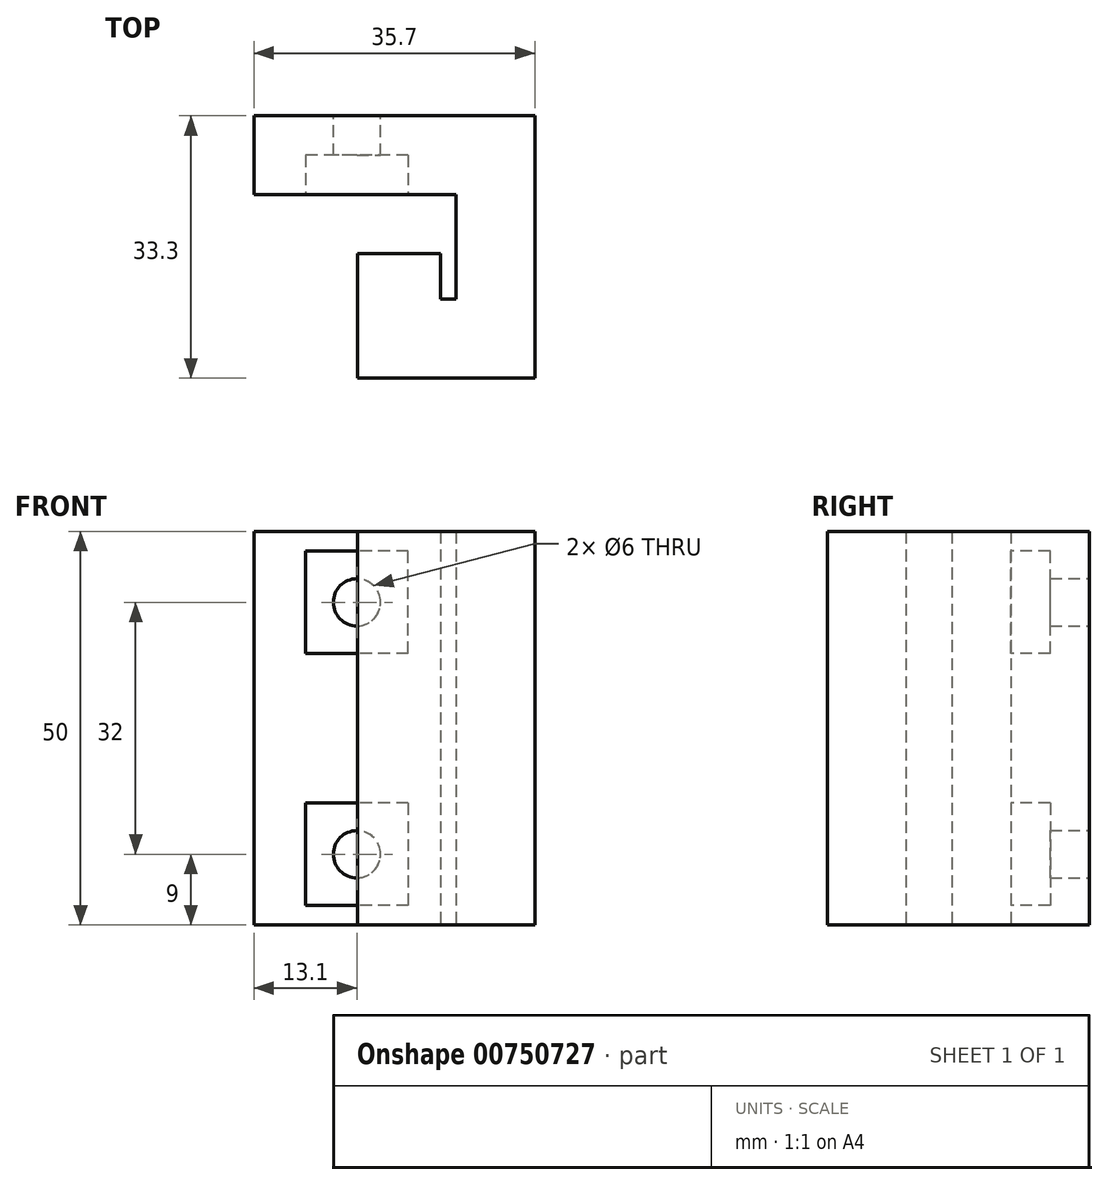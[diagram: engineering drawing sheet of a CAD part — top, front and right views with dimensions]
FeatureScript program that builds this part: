
annotation { "Feature Type Name" : "Feature", "Feature Type Description" : "" }
export const myFeature = defineFeature(function(context is Context, id is Id, definition is map)
    precondition{}
    {
        {
            var Q0;
            Q0=qCreatedBy(makeId("Top.planeOp"),FACE);
            var sketch = newSketch(context, id + "F0", { "sketchPlane" : qUnion([Q0])});
            skPoint(sketch, "E0.middle", {"position": v(0, 0) * mm});
            skLineSegment(sketch, "E1", {"start": v(22.5, 33.3) * mm, "end": v(22.5, 0) * mm});
            skLineSegment(sketch, "E2", {"start": v(22.5, 0) * mm, "end": v(0, 0) * mm});
            skLineSegment(sketch, "E3", {"start": v(12.5, 10) * mm, "end": v(12.5, 23.3) * mm});
            skLineSegment(sketch, "E4", {"start": v(12.5, 23.3) * mm, "end": v(-13.2, 23.3) * mm});
            skLineSegment(sketch, "E5", {"start": v(12.5, 10) * mm, "end": v(10.5, 10) * mm});
            skLineSegment(sketch, "E6", {"start": v(10.5, 10) * mm, "end": v(10.5, 15.8) * mm});
            skLineSegment(sketch, "E7", {"start": v(10.5, 15.8) * mm, "end": v(0, 15.8) * mm});
            skLineSegment(sketch, "E8", {"start": v(0, 15.8) * mm, "end": v(0, 0) * mm});
            skLineSegment(sketch, "E9", {"start": v(22.5, 33.3) * mm, "end": v(-13.2, 33.3) * mm});
            skLineSegment(sketch, "E10", {"start": v(22.5, 16.65) * mm, "end": v(12.5, 16.65) * mm, "construction": true});
            skLineSegment(sketch, "E11", {"start": v(11.5, 10) * mm, "end": v(11.5, 0) * mm, "construction": true});
            skLineSegment(sketch, "E12", {"start": v(-13.2, 33.3) * mm, "end": v(-13.2, 23.3) * mm});
            skSolve(sketch);
        }
        {
            var Q0;
            Q0 = qSketchRegion(id + "F0", true);
            extrude(context, id + "F1", {"entities" : qUnion([Q0]), "endBound" : BoundingType.SYMMETRIC, "depth" : 50 * mm, "offsetDistance" : 25 * mm});
        }
        {
            var Q0;
            Q0=makeQuery(id+"F1.opExtrude","SWEPT_FACE",FACE,{"disambiguationData":[OSD([sQuery(id+"F0.wireOp",EDGE,"E9")])]});
            var sketch = newSketch(context, id + "F2", { "sketchPlane" : qUnion([Q0])});
            skCircle(sketch, "E13", {"center": v(0.1, -16) * mm, "radius": 3 * mm});
            skCircle(sketch, "E14.MirrorC", {"center": v(0.1, 16) * mm, "radius": 3 * mm});
            skSolve(sketch);
        }
        {
            var Q0;
            Q0 = qSketchRegion(id + "F2", true);
            var Q1;
            Q1=makeQuery(id+"F1.opExtrude","SWEPT_FACE",FACE,{"disambiguationData":[OSD([sQuery(id+"F0.wireOp",EDGE,"E4")])]});
            extrude(context, id + "F3", {"entities" : qUnion([Q0]), "operationType" : NewBodyOperationType.REMOVE, "endBound" : BoundingType.UP_TO_SURFACE, "oppositeDirection" : true, "depth" : 25 * mm, "endBoundEntityFace" : qUnion([Q1]), "offsetDistance" : 25 * mm});
        }
        {
            var Q0;
            Q0=makeQuery(id+"F1.opExtrude","SWEPT_FACE",FACE,{"disambiguationData":[OSD([sQuery(id+"F0.wireOp",EDGE,"E4")])]});
            var sketch = newSketch(context, id + "F4", { "sketchPlane" : qUnion([Q0])});
            skLineSegment(sketch, "E15.bottom", {"start": v(6.4, 9.5) * mm, "end": v(-6.6, 9.5) * mm});
            skLineSegment(sketch, "E15.top", {"start": v(6.4, 22.5) * mm, "end": v(-6.6, 22.5) * mm});
            skLineSegment(sketch, "E15.left", {"start": v(6.4, 9.5) * mm, "end": v(6.4, 22.5) * mm});
            skLineSegment(sketch, "E15.right", {"start": v(-6.6, 9.5) * mm, "end": v(-6.6, 22.5) * mm});
            skPoint(sketch, "E15.middle", {"position": v(-0.1, 16) * mm});
            skLineSegment(sketch, "E16.MirrorCS", {"start": v(-6.6, -9.5) * mm, "end": v(-6.6, -22.5) * mm});
            skLineSegment(sketch, "E17.MirrorCS", {"start": v(6.4, -22.5) * mm, "end": v(-6.6, -22.5) * mm});
            skLineSegment(sketch, "E18.MirrorCS", {"start": v(6.4, -9.5) * mm, "end": v(6.4, -22.5) * mm});
            skLineSegment(sketch, "E19.MirrorCS", {"start": v(6.4, -9.5) * mm, "end": v(-6.6, -9.5) * mm});
            skSolve(sketch);
        }
        {
            var Q0;
            Q0 = qSketchRegion(id + "F4", true);
            extrude(context, id + "F5", {"entities" : qUnion([Q0]), "operationType" : NewBodyOperationType.REMOVE, "oppositeDirection" : true, "depth" : 5 * mm, "offsetDistance" : 25 * mm});
        }
    });
